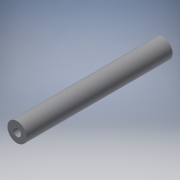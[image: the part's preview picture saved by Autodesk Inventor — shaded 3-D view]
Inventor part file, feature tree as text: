
AUTODESK INVENTOR PART (.ipt)
format: ipt  version: 2017 (Build 210142000, 142)  size: 100,864 bytes
history: native  units: in
note: dims shown in document units (in); Inventor stores cm internally (conversion verified against a paired STEP export)
features: sketch x2, extrude x1, hole x1, thicken_offset x1
ambient origin geometry x8: Origin, YZ Plane, XZ Plane, XY Plane, X Axis, Y Axis, Z Axis, Center Point
bodies: Solid1 (feature_tree)
feature tree (5):
  extrude  "Extrusion1"  Depth=3.568in TaperAngle=0.0deg
  hole  "Hole1"  [1 undecoded]
  thicken_offset  "Thicken1"
  sketch  "Sketch1"  dims[d1=0.35in d2=3.568in d3=0.0in]
  sketch  "Sketch2"  dims[d5=0.145in d6=0.38in d7=0.375in d8=0.25in d9=0.5635in d10=1.496in d11=0.8108in d12=0.908in d13=0.908in]
note: 1 required parameter value undecoded (feature->parameter linkage not recoverable at this tier; creation-order binding heuristic only, values carry confidence <= 0.55)
